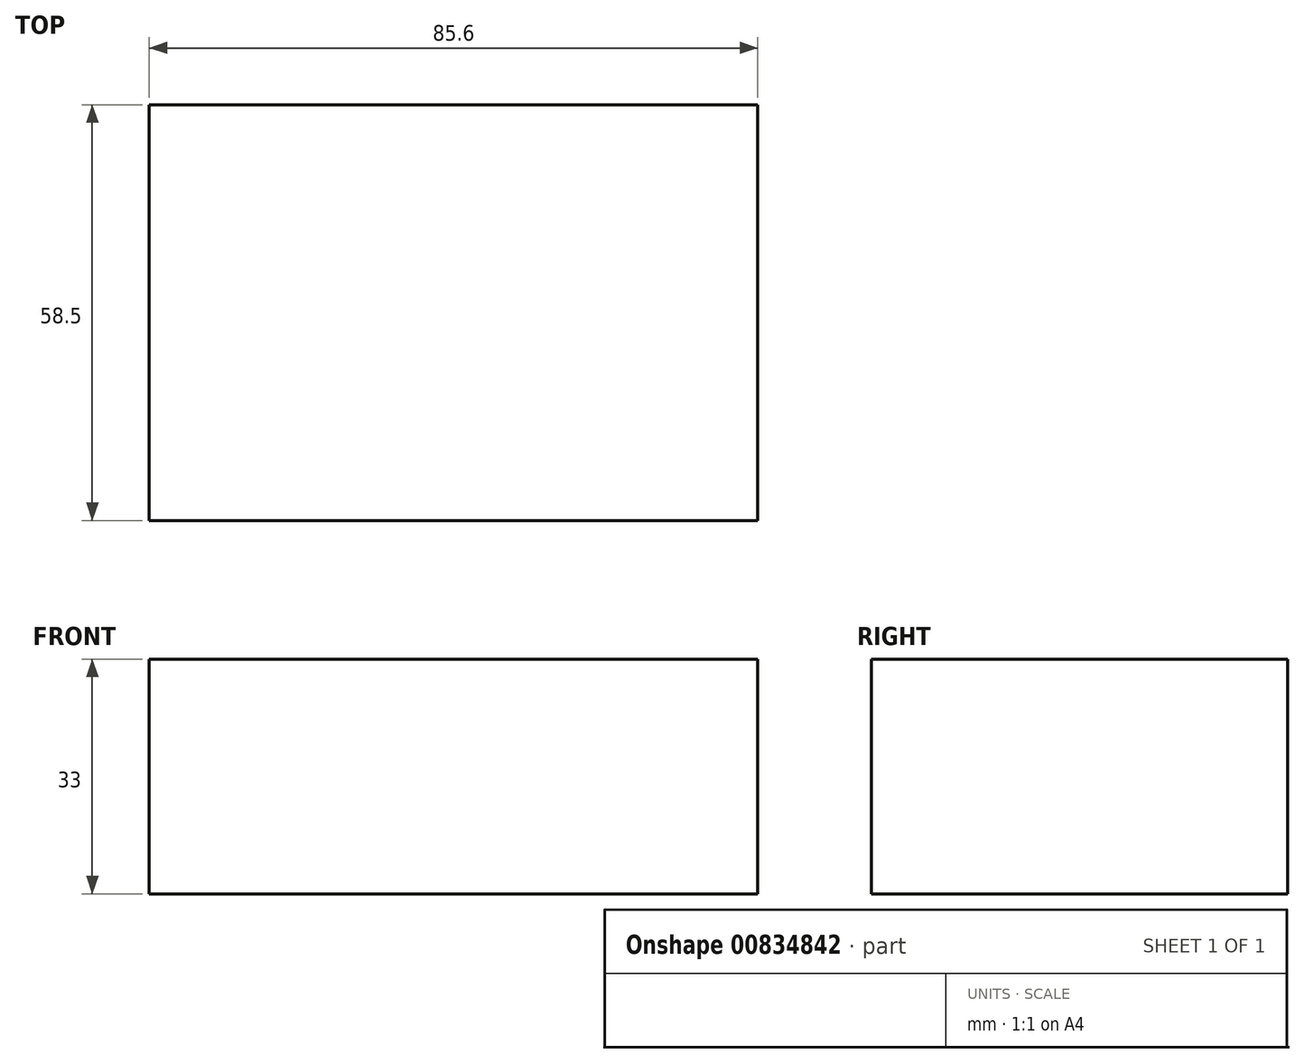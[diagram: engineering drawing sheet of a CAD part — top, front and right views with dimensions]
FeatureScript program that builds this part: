
annotation { "Feature Type Name" : "Feature", "Feature Type Description" : "" }
export const myFeature = defineFeature(function(context is Context, id is Id, definition is map)
    precondition{}
    {
        {
            var Q0;
            Q0=qCreatedBy(makeId("Top.planeOp"),FACE);
            var sketch = newSketch(context, id + "F0", { "sketchPlane" : qUnion([Q0])});
            skLineSegment(sketch, "E0.bottom", {"start": v(-85.6, 58.5) * mm, "end": v(0, 58.5) * mm});
            skLineSegment(sketch, "E0.top", {"start": v(-85.6, 0) * mm, "end": v(0, 0) * mm});
            skLineSegment(sketch, "E0.left", {"start": v(-85.6, 58.5) * mm, "end": v(-85.6, 0) * mm});
            skLineSegment(sketch, "E0.right", {"start": v(0, 58.5) * mm, "end": v(0, 0) * mm});
            skSolve(sketch);
        }
        {
            var Q0;
            Q0 = qSketchRegion(id + "F0", true);
            extrude(context, id + "F1", {"entities" : qUnion([Q0]), "depth" : 33 * mm, "offsetDistance" : 25 * mm});
        }
    });
